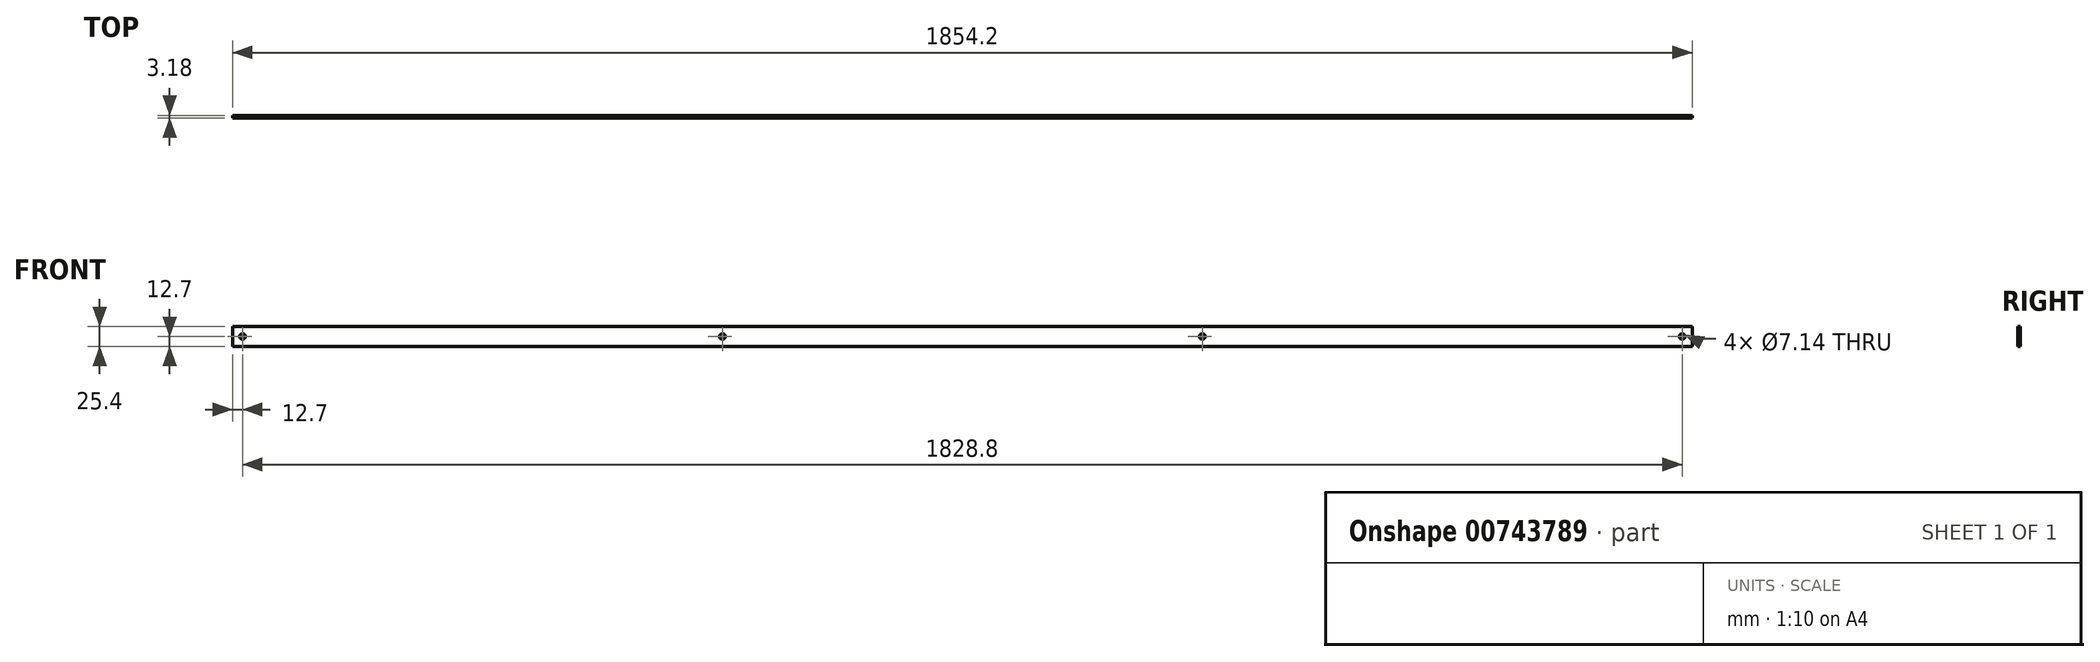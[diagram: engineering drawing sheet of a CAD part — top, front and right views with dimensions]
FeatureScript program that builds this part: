
annotation { "Feature Type Name" : "Feature", "Feature Type Description" : "" }
export const myFeature = defineFeature(function(context is Context, id is Id, definition is map)
    precondition{}
    {
        {
            var Q0;
            Q0=qCreatedBy(makeId("Front.planeOp"),FACE);
            var sketch = newSketch(context, id + "F0", { "sketchPlane" : qUnion([Q0])});
            skLineSegment(sketch, "E0.bottom", {"start": v(0, 0) * mm, "end": v(-1854.2, 0) * mm});
            skLineSegment(sketch, "E0.top", {"start": v(0, 25.4) * mm, "end": v(-1854.2, 25.4) * mm});
            skLineSegment(sketch, "E0.left", {"start": v(0, 0) * mm, "end": v(0, 25.4) * mm});
            skLineSegment(sketch, "E0.right", {"start": v(-1854.2, 0) * mm, "end": v(-1854.2, 25.4) * mm});
            skCircle(sketch, "E1", {"center": v(-12.7, 12.7) * mm, "radius": 3.57 * mm});
            skCircle(sketch, "E2.1.0.0", {"center": v(-622.3, 12.7) * mm, "radius": 3.57 * mm});
            skCircle(sketch, "E2.2.0.0", {"center": v(-1231.9, 12.7) * mm, "radius": 3.57 * mm});
            skCircle(sketch, "E2.3.0.0", {"center": v(-1841.5, 12.7) * mm, "radius": 3.57 * mm});
            skLineSegment(sketch, "E2.direction1", {"start": v(-12.7, 12.7) * mm, "end": v(-622.3, 12.7) * mm, "construction": true});
            skSolve(sketch);
        }
        {
            var Q0;
            Q0=qSketchRegion(id+"F0",true);
            extrude(context, id + "F1", {"entities" : qUnion([Q0]), "depth" : 3.17 * mm, "offsetDistance" : 25.4 * mm});
        }
    });
